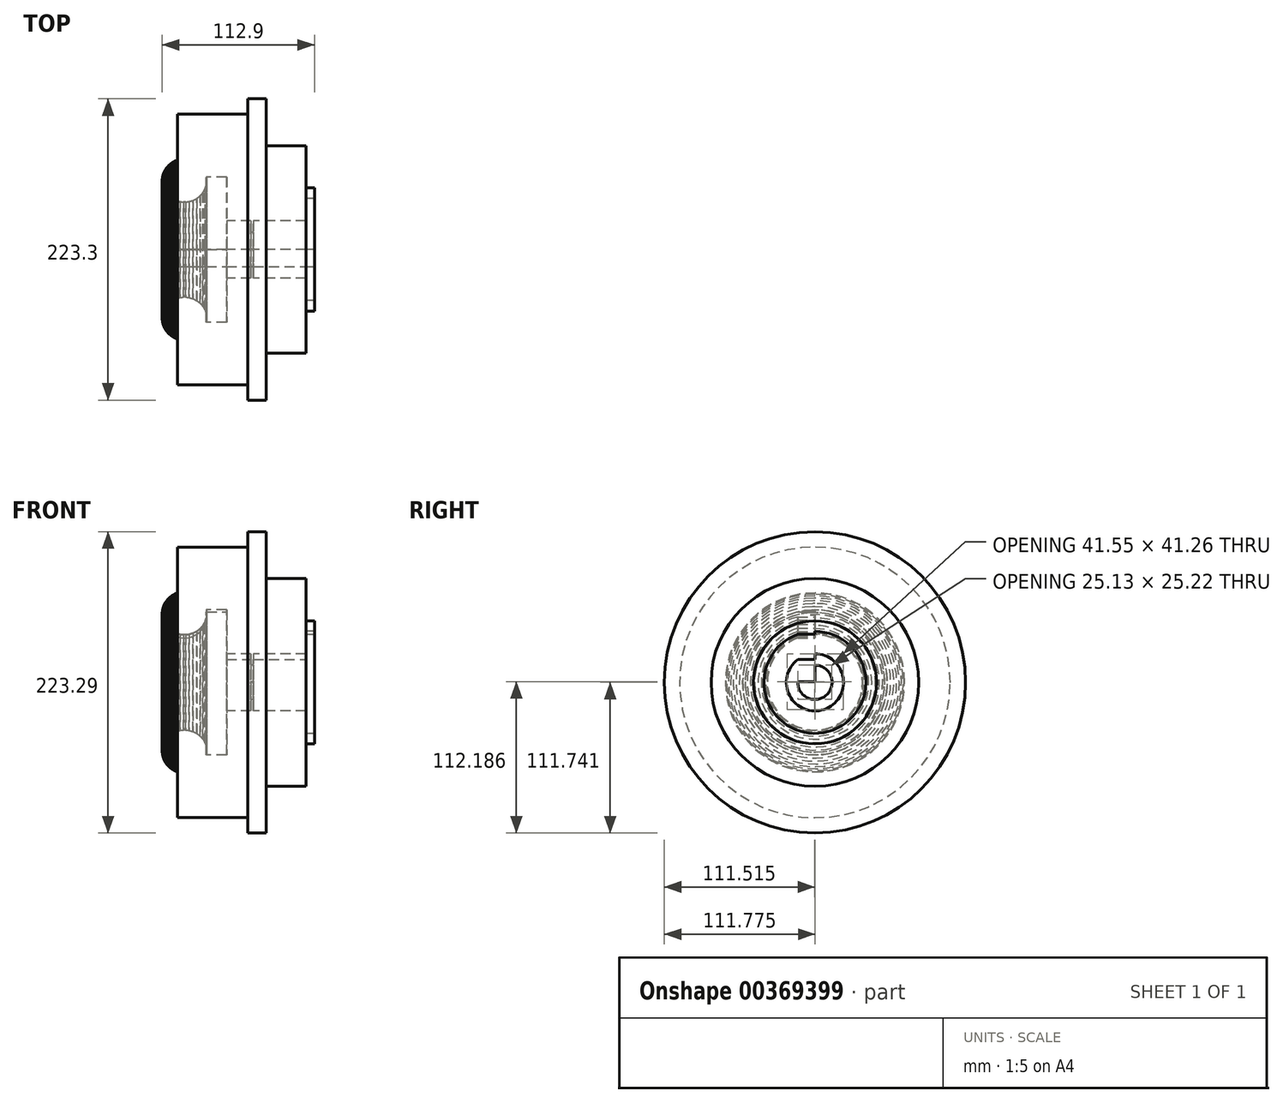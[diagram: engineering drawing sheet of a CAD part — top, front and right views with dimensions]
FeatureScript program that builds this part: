
annotation { "Feature Type Name" : "Feature", "Feature Type Description" : "" }
export const myFeature = defineFeature(function(context is Context, id is Id, definition is map)
    precondition{}
    {
        {
            var Q0;
            Q0=qCreatedBy(makeId("Front.planeOp"),FACE);
            var sketch = newSketch(context, id + "F0", { "sketchPlane" : qUnion([Q0])});
            skLineSegment(sketch, "E0", {"start": v(56.46, -11.85) * mm, "end": v(50.2, -11.85) * mm});
            skLineSegment(sketch, "E1", {"start": v(50.2, -11.85) * mm, "end": v(50.2, 20.19) * mm});
            skLineSegment(sketch, "E2", {"start": v(50.2, 20.19) * mm, "end": v(20.74, 20.19) * mm});
            skLineSegment(sketch, "E3", {"start": v(20.74, 20.19) * mm, "end": v(20.74, 55.24) * mm});
            skLineSegment(sketch, "E4", {"start": v(20.74, 55.24) * mm, "end": v(7.12, 55.24) * mm});
            skLineSegment(sketch, "E5", {"start": v(7.12, 55.24) * mm, "end": v(7.12, 43.79) * mm});
            skLineSegment(sketch, "E6", {"start": v(7.12, 43.79) * mm, "end": v(-45, 43.79) * mm});
            skLineSegment(sketch, "E7", {"start": v(-45, 43.79) * mm, "end": v(-45, 9.45) * mm});
            skLineSegment(sketch, "E8", {"start": v(-45, 9.45) * mm, "end": v(-45.62, 9.25) * mm});
            skLineSegment(sketch, "E9", {"start": v(-45.62, 9.25) * mm, "end": v(-47.4, 8.46) * mm});
            skLineSegment(sketch, "E10", {"start": v(-47.4, 8.46) * mm, "end": v(-49.6, 7.12) * mm});
            skLineSegment(sketch, "E11", {"start": v(-49.6, 7.12) * mm, "end": v(-51.55, 5.47) * mm});
            skLineSegment(sketch, "E12", {"start": v(-51.55, 5.47) * mm, "end": v(-53.23, 3.54) * mm});
            skLineSegment(sketch, "E13", {"start": v(-53.23, 3.54) * mm, "end": v(-54.59, 1.37) * mm});
            skLineSegment(sketch, "E14", {"start": v(-54.59, 1.37) * mm, "end": v(-55.6, -1.01) * mm});
            skLineSegment(sketch, "E15", {"start": v(-55.6, -1.01) * mm, "end": v(-56.24, -3.57) * mm});
            skLineSegment(sketch, "E16", {"start": v(-56.24, -3.57) * mm, "end": v(-56.46, -5.6) * mm});
            skLineSegment(sketch, "E17", {"start": v(-56.46, -5.6) * mm, "end": v(-56.46, -6.27) * mm});
            skLineSegment(sketch, "E18", {"start": v(-56.46, -6.27) * mm, "end": v(-56.46, -7.1) * mm});
            skLineSegment(sketch, "E19", {"start": v(-56.46, -7.1) * mm, "end": v(-56.13, -9.6) * mm});
            skLineSegment(sketch, "E20", {"start": v(-56.13, -9.6) * mm, "end": v(-55.17, -12.69) * mm});
            skLineSegment(sketch, "E21", {"start": v(-55.17, -12.69) * mm, "end": v(-53.65, -15.5) * mm});
            skLineSegment(sketch, "E22", {"start": v(-53.65, -15.5) * mm, "end": v(-51.63, -17.94) * mm});
            skLineSegment(sketch, "E23", {"start": v(-51.63, -17.94) * mm, "end": v(-49.19, -19.96) * mm});
            skLineSegment(sketch, "E24", {"start": v(-49.19, -19.96) * mm, "end": v(-46.38, -21.48) * mm});
            skLineSegment(sketch, "E25", {"start": v(-46.38, -21.48) * mm, "end": v(-43.28, -22.44) * mm});
            skLineSegment(sketch, "E26", {"start": v(-43.28, -22.44) * mm, "end": v(-40.79, -22.78) * mm});
            skLineSegment(sketch, "E27", {"start": v(-40.79, -22.78) * mm, "end": v(-39.95, -22.78) * mm});
            skLineSegment(sketch, "E28", {"start": v(-39.95, -22.78) * mm, "end": v(-39.12, -22.78) * mm});
            skLineSegment(sketch, "E29", {"start": v(-39.12, -22.78) * mm, "end": v(-36.63, -22.44) * mm});
            skLineSegment(sketch, "E30", {"start": v(-36.63, -22.44) * mm, "end": v(-33.53, -21.48) * mm});
            skLineSegment(sketch, "E31", {"start": v(-33.53, -21.48) * mm, "end": v(-30.73, -19.96) * mm});
            skLineSegment(sketch, "E32", {"start": v(-30.73, -19.96) * mm, "end": v(-28.28, -17.95) * mm});
            skLineSegment(sketch, "E33", {"start": v(-28.28, -17.95) * mm, "end": v(-26.27, -15.5) * mm});
            skLineSegment(sketch, "E34", {"start": v(-26.27, -15.5) * mm, "end": v(-24.74, -12.7) * mm});
            skLineSegment(sketch, "E35", {"start": v(-24.74, -12.7) * mm, "end": v(-23.78, -9.6) * mm});
            skLineSegment(sketch, "E36", {"start": v(-23.78, -9.6) * mm, "end": v(-23.44, -7.1) * mm});
            skLineSegment(sketch, "E37", {"start": v(-23.44, -7.1) * mm, "end": v(-23.44, -6.27) * mm});
            skLineSegment(sketch, "E38", {"start": v(-23.44, -6.27) * mm, "end": v(-23.44, -5.56) * mm});
            skLineSegment(sketch, "E39", {"start": v(-23.44, -5.56) * mm, "end": v(-23.66, -3.64) * mm});
            skLineSegment(sketch, "E40", {"start": v(-23.66, -3.64) * mm, "end": v(-23.7, -3.41) * mm});
            skLineSegment(sketch, "E41", {"start": v(-23.7, -3.41) * mm, "end": v(-8.73, -3.41) * mm});
            skLineSegment(sketch, "E42", {"start": v(-8.73, -3.41) * mm, "end": v(-8.73, -38.73) * mm});
            skLineSegment(sketch, "E43", {"start": v(-8.73, -38.73) * mm, "end": v(9.26, -38.73) * mm});
            skLineSegment(sketch, "E44", {"start": v(9.26, -38.73) * mm, "end": v(9.26, -55.24) * mm});
            skLineSegment(sketch, "E45", {"start": v(9.26, -55.24) * mm, "end": v(11.16, -55.24) * mm});
            skLineSegment(sketch, "E46", {"start": v(11.16, -55.24) * mm, "end": v(11.16, -38.73) * mm});
            skLineSegment(sketch, "E47", {"start": v(11.16, -38.73) * mm, "end": v(50.16, -38.73) * mm});
            skLineSegment(sketch, "E48", {"start": v(50.16, -38.73) * mm, "end": v(50.16, -20.06) * mm});
            skLineSegment(sketch, "E49", {"start": v(50.16, -20.06) * mm, "end": v(56.44, -20.06) * mm});
            skLineSegment(sketch, "E50", {"start": v(56.44, -20.06) * mm, "end": v(56.44, -11.85) * mm});
            skLineSegment(sketch, "E51", {"start": v(56.44, -11.85) * mm, "end": v(56.46, -11.85) * mm});
            skLineSegment(sketch, "E52", {"start": v(0, -55.68) * mm, "end": v(76.7, -55.68) * mm, "construction": true});
            skSolve(sketch);
        }
        {
            var Q0;
            Q0=makeQuery(id+"F0.imprint","IMPRINT",FACE,{"disambiguationData":[TD([[makeQuery(id+"F0.imprint","IMPRINT",EDGE,{"derivedFrom":sQuery(id+"F0.wireOp",EDGE,"E0")}),1.0]])]});
            extrude(context, id + "F1", {"entities" : qUnion([Q0]), "depth" : 12.7 * mm});
        }
        {
            var Q0;
            Q0=makeQuery(id+"F1.opExtrude","CAP_FACE",FACE,{"disambiguationData":[OSD([sQuery(id+"F0.wireOp",EDGE,"E0"),sQuery(id+"F0.wireOp",EDGE,"E1"),sQuery(id+"F0.wireOp",EDGE,"E2"),sQuery(id+"F0.wireOp",EDGE,"E3"),sQuery(id+"F0.wireOp",EDGE,"E4"),sQuery(id+"F0.wireOp",EDGE,"E5"),sQuery(id+"F0.wireOp",EDGE,"E6"),sQuery(id+"F0.wireOp",EDGE,"E7"),sQuery(id+"F0.wireOp",EDGE,"E8"),sQuery(id+"F0.wireOp",EDGE,"E9"),sQuery(id+"F0.wireOp",EDGE,"E10"),sQuery(id+"F0.wireOp",EDGE,"E11"),sQuery(id+"F0.wireOp",EDGE,"E12"),sQuery(id+"F0.wireOp",EDGE,"E13"),sQuery(id+"F0.wireOp",EDGE,"E14"),sQuery(id+"F0.wireOp",EDGE,"E15"),sQuery(id+"F0.wireOp",EDGE,"E16"),sQuery(id+"F0.wireOp",EDGE,"E17"),sQuery(id+"F0.wireOp",EDGE,"E18"),sQuery(id+"F0.wireOp",EDGE,"E19"),sQuery(id+"F0.wireOp",EDGE,"E20"),sQuery(id+"F0.wireOp",EDGE,"E21"),sQuery(id+"F0.wireOp",EDGE,"E22"),sQuery(id+"F0.wireOp",EDGE,"E23"),sQuery(id+"F0.wireOp",EDGE,"E24"),sQuery(id+"F0.wireOp",EDGE,"E25"),sQuery(id+"F0.wireOp",EDGE,"E26"),sQuery(id+"F0.wireOp",EDGE,"E27"),sQuery(id+"F0.wireOp",EDGE,"E28"),sQuery(id+"F0.wireOp",EDGE,"E29"),sQuery(id+"F0.wireOp",EDGE,"E30"),sQuery(id+"F0.wireOp",EDGE,"E31"),sQuery(id+"F0.wireOp",EDGE,"E32"),sQuery(id+"F0.wireOp",EDGE,"E33"),sQuery(id+"F0.wireOp",EDGE,"E34"),sQuery(id+"F0.wireOp",EDGE,"E35"),sQuery(id+"F0.wireOp",EDGE,"E36"),sQuery(id+"F0.wireOp",EDGE,"E37"),sQuery(id+"F0.wireOp",EDGE,"E38"),sQuery(id+"F0.wireOp",EDGE,"E39"),sQuery(id+"F0.wireOp",EDGE,"E40"),sQuery(id+"F0.wireOp",EDGE,"E41"),sQuery(id+"F0.wireOp",EDGE,"E42"),sQuery(id+"F0.wireOp",EDGE,"E43"),sQuery(id+"F0.wireOp",EDGE,"E44"),sQuery(id+"F0.wireOp",EDGE,"E45"),sQuery(id+"F0.wireOp",EDGE,"E46"),sQuery(id+"F0.wireOp",EDGE,"E47"),sQuery(id+"F0.wireOp",EDGE,"E48"),sQuery(id+"F0.wireOp",EDGE,"E49"),sQuery(id+"F0.wireOp",EDGE,"E50")])],"isStart":false});
            var Q1;
            Q1=sQuery(id+"F0.wireOp",EDGE,"E52");
            revolve(context, id + "F2", {"operationType" : NewBodyOperationType.ADD, "entities" : qUnion([Q0]), "axis" : qUnion([Q1]), "revolveType" : RevolveType.FULL});
        }
    });
